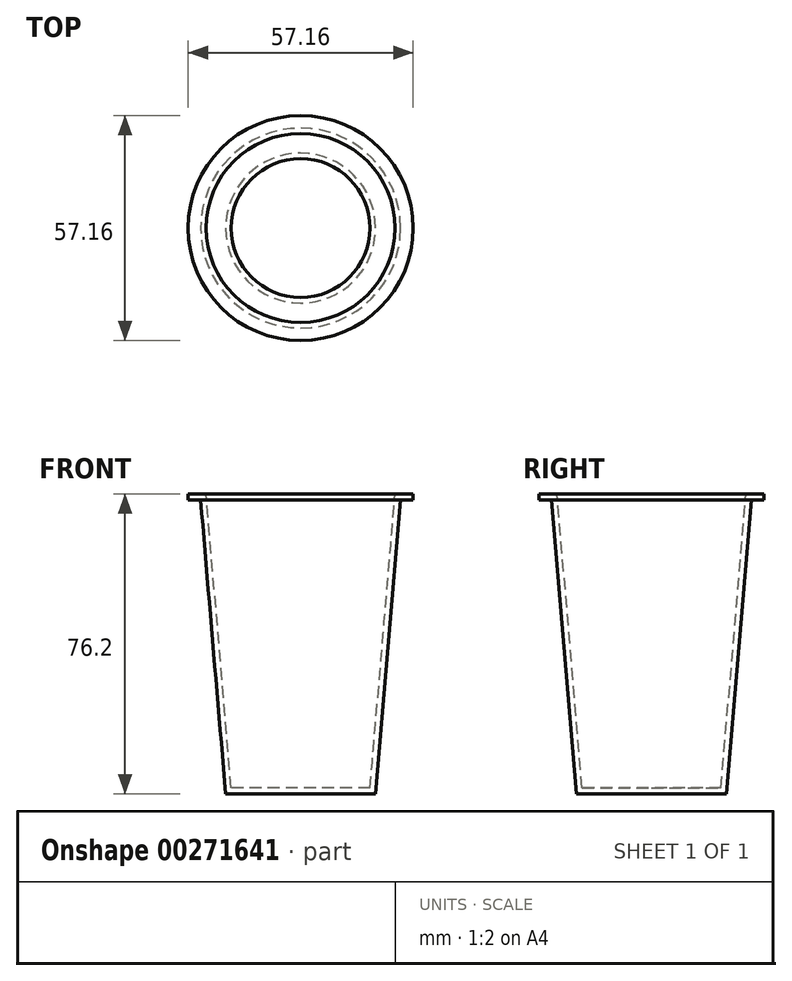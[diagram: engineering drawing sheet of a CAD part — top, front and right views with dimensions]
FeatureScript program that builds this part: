
annotation { "Feature Type Name" : "Feature", "Feature Type Description" : "" }
export const myFeature = defineFeature(function(context is Context, id is Id, definition is map)
    precondition{}
    {
        {
            var Q0;
            Q0=qCreatedBy(makeId("Front.planeOp"),FACE);
            var sketch = newSketch(context, id + "F0", { "sketchPlane" : qUnion([Q0])});
            skLineSegment(sketch, "E0", {"start": v(0, 0) * mm, "end": v(0, 76.2) * mm});
            skLineSegment(sketch, "E1", {"start": v(0, 76.2) * mm, "end": v(28.58, 76.2) * mm});
            skLineSegment(sketch, "E2", {"start": v(28.58, 76.2) * mm, "end": v(28.58, 74.68) * mm});
            skLineSegment(sketch, "E3", {"start": v(28.58, 74.68) * mm, "end": v(25.4, 74.68) * mm});
            skLineSegment(sketch, "E4", {"start": v(25.4, 74.68) * mm, "end": v(19.05, 0) * mm});
            skLineSegment(sketch, "E5", {"start": v(19.05, 0) * mm, "end": v(0, 0) * mm});
            skLineSegment(sketch, "E6", {"start": v(0, 0) * mm, "end": v(0, 103.23) * mm, "construction": true});
            skSolve(sketch);
        }
        {
            var Q0;
            Q0 = qSketchRegion(id + "F0", true);
            var Q1;
            Q1=sQuery(id+"F0.wireOp",EDGE,"E6");
            revolve(context, id + "F1", {"entities" : qUnion([Q0]), "axis" : qUnion([Q1]), "revolveType" : RevolveType.FULL});
        }
        {
            var Q0;
            Q0=makeQuery(id+"F1.opRevolve","SWEPT_FACE",FACE,{"disambiguationData":[OSD([sQuery(id+"F0.wireOp",EDGE,"E1")])]});
            shell(context, id + "F2", {"entities" : qUnion([Q0]), "thickness" : 1.52 * mm});
        }
    });
